# Revit family: LEGRAND_PRISES_NON_VERROUILLEES_SAILLIES_IP44_230
name_source: partatom
category: Installations électriques
revit_build: Autodesk Revit 2018 (Build: 20170223_1515(x64)
units: mm (PartAtom-declared; Revit-internal decimal feet)

## family parameters
Conserver l'orientation des annotations = Non
Cote de connecteur circulaire = Utiliser le diamètre
Couper avec des vides une fois chargée = Non
Hôte = Face
Partagée = Non
Point de calcul de pièce = Non
Type d'élément = Normal

## types (19) — shared parameters
Conditions Générale d'Utilisation = https://export.legrand.com
Couleur caractéristique = bleu
Description = Prise au standard international pour montage encastré ou saillie avec accessoire permet la connexion d'appareils de puissance
Dia bouchon = 50 mm  [stored 0.164042 ft]
Elévation par défaut = 1000 mm  [stored 3.28084 ft]
Fabricant = Legrand
RAY BOUCHON = 25 mm  [stored 0.082021 ft]
Ray = 25 mm  [stored 0.082021 ft]
Standard CEI ou NFC = CEI
Température maximale d'installation = 40°C
Température maximum d'utilisation = 100°C
Température minimum d'installation = -20°C
Température minimum d'utilisation = -50°C
Tension V = 230 V  50/60 Hz  bleu
classe de protection IP = IP44
installation Encastrée E ou Saillie S = encastré et saillie
type de raccordement = bornes à vis

## per-type parameters (varying)
| type | Intensité A | Modèle | Nombre de pôles | Position de la Terre h | entraxe de fixation horizontal mm | entraxe de fixation vertical mm | h1 | hauteur mm | largeur mm | matériau du boitier | profondeur d'encastrement mm | profondeur mm | résistance aux chocs IK | sans halogène |
| Socle tableau Hypra   IP44   16 A   200/250 V   2P+T   plast saillie boitier passage | 16 A | 052022 | 3 | 6 | 52 mm | 60 mm | 109 mm | 182 mm | 86 mm | plastique | 75 mm | 115 mm | 09 | Oui |
| Socle tableau Hypra   IP44   16 A   200/250 V   3P+T   plast saillie boitier passage | 16 A | 052023 | 4 | 9 | 60 mm | 70 mm | 127 mm | 212 mm | 100 mm  [stored 0.328084 ft] | plastique | 77 mm | 117 mm | 09 | Oui |
| Socle tableau Hypra   IP44   16 A   200/250 V   3P+N+T   plast saillie boitier passage | 16 A | 052024 | 5 | 9 | 60 mm | 70 mm | 127 mm | 212 mm | 100 mm  [stored 0.328084 ft] | plastique | 77 mm | 121 mm | 09 | Oui |
| Socle de tableau Hypra   IP44   16 A   200/250 V   2P+T   métal saillie boitier simple | 16 A | 052032 | 3 | 6 | 52 mm | 60 mm | 64 mm | 106 mm | 74 mm | métal | 58 mm | 98 mm | 10 | Oui |
| Socle de tableau Hypra   IP44   16 A   200/250 V   3P+N+T   métal saillie boitier simple | 16 A | 052034 | 5 | 9 | 60 mm | 70 mm | 73 mm | 122 mm  [stored 0.400262 ft] | 96 mm  [stored 0.314961 ft] | métal | 60 mm | 104 mm | 10 | Oui |
| Socle tableau Hypra   IP44   32 A   200/250 V   2P+T   plast saillie boitier passage | 32 A | 052718 | 3 | 6 | 70 mm | 70 mm | 97 mm | 162 mm | 102 mm | plastique | 90 mm  [stored 0.295276 ft] | 143 mm | 09 | Oui |
| Socle tableau Hypra   IP44   32 A   200/250 V   3P+T   plast saillie boitier passage | 32 A | 052719 | 4 | 9 | 70 mm | 70 mm | 97 mm | 162 mm | 102 mm | plastique | 90 mm  [stored 0.295276 ft] | 143 mm | 09 | Oui |
| Socle tableau Hypra   IP44   32 A   200/250 V   3P+N+T   plast saillie boitier passage | 32 A | 052720 | 5 | 9 | 70 mm | 70 mm | 97 mm | 162 mm | 102 mm | plastique | 90 mm  [stored 0.295276 ft] | 146 mm  [stored 0.479003 ft] | 09 | Oui |
| Socle tableau Hypra   IP44   32 A   200/250 V   2P+T   métal saillie boitier simple | 32 A | 052732 | 5 | 9 | 70 mm | 80 mm | 97 mm | 162 mm | 102 mm | métal | 90 mm  [stored 0.295276 ft] | 143 mm | 09 | Oui |
| Socle tableau Hypra   IP44   32 A   200/250 V   3P+T   métal saillie boitier simple | 32 A | 052733 | 4 | 9 | 70 mm | 80 mm | 97 mm | 162 mm | 102 mm | métal | 90 mm  [stored 0.295276 ft] | 143 mm | 10 | Oui |
| Socle tableau Hypra   IP44   63 A   200/250 V   2P+T   plast saillie boitier passage | 63 A | 053622 | 3 | 6 | 77 mm | 85 mm | 180 mm  [stored 0.590551 ft] | 300 mm | 170 mm | plastique | 150 mm | 220 mm | 09 | Non |
| Socle tableau Hypra   IP44   63 A   200/250 V   3P+T   plast saillie boitier passage | 63 A | 053623 | 4 | 9 | 77 mm | 85 mm | 180 mm  [stored 0.590551 ft] | 300 mm | 170 mm | plastique | 150 mm | 220 mm | 09 | Non |
| Socle de tableau Hypra   IP44   16 A   200/250 V   3P+T   métal saillie boitier simple | 16 A | 052033 | 4 | 9 | 60 mm | 70 mm | 73 mm | 122 mm  [stored 0.400262 ft] | 96 mm  [stored 0.314961 ft] | métal | 60 mm | 100 mm  [stored 0.328084 ft] | 10 | Oui |
| Socle tableau Hypra   IP44   16 A   200/250 V   2P+T   plast saillie boitier simple | 16 A | 052022 | 3 | 6 | 52 mm | 60 mm | 64 mm | 106 mm | 74 mm | plastique | 58 mm | 98 mm | 09 | Oui |
| Socle tableau Hypra   IP44   16 A   200/250 V   3P+T   plast saillie boitier simple | 16 A | 052023 | 4 | 9 | 60 mm | 70 mm | 73 mm | 122 mm  [stored 0.400262 ft] | 96 mm  [stored 0.314961 ft] | plastique | 60 mm | 100 mm  [stored 0.328084 ft] | 09 | Oui |
| Socle tableau Hypra   IP44   16 A   200/250 V   3P+N+T   plast saillie boitier simple | 16 A | 052024 | 5 | 9 | 60 mm | 70 mm | 73 mm | 122 mm  [stored 0.400262 ft] | 96 mm  [stored 0.314961 ft] | plastique | 60 mm | 104 mm | 09 | Oui |
| Socle tableau Hypra   IP44   32 A   200/250 V   2P+T   plast saillie boitier simple | 32 A | 052718 | 3 | 6 | 70 mm | 70 mm | 97 mm | 162 mm | 102 mm | plastique | 90 mm  [stored 0.295276 ft] | 143 mm | 09 | Oui |
| Socle tableau Hypra   IP44   32 A   200/250 V   3P+T   plast saillie boitier simple | 32 A | 052719 | 4 | 9 | 70 mm | 70 mm | 97 mm | 162 mm | 102 mm | plastique | 90 mm  [stored 0.295276 ft] | 143 mm | 09 | Oui |
| Socle tableau Hypra   IP44   32 A   200/250 V   3P+N+T   plast saillie boitier simple | 32 A | 052720 | 5 | 9 | 70 mm | 70 mm | 97 mm | 162 mm | 102 mm | plastique | 90 mm  [stored 0.295276 ft] | 146 mm  [stored 0.479003 ft] | 09 | Oui |

note: [stored X ft] marks values corroborated as IEEE doubles in the binary element streams (Revit-internal decimal feet)
